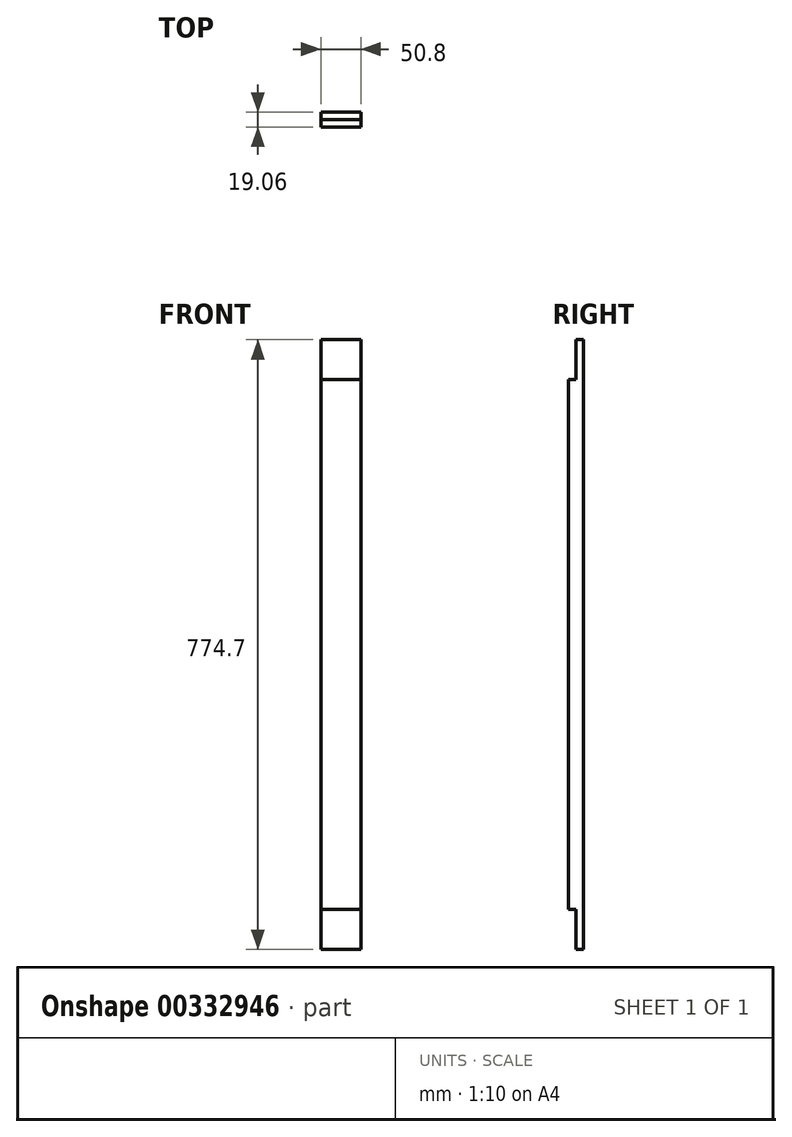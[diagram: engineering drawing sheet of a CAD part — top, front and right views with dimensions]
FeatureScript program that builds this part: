
annotation { "Feature Type Name" : "Feature", "Feature Type Description" : "" }
export const myFeature = defineFeature(function(context is Context, id is Id, definition is map)
    precondition{}
    {
        {
            var Q0;
            Q0=qCreatedBy(makeId("Top.planeOp"),FACE);
            var sketch = newSketch(context, id + "F0", { "sketchPlane" : qUnion([Q0])});
            skLineSegment(sketch, "E0.bottom", {"start": v(25.4, 9.53) * mm, "end": v(-25.4, 9.53) * mm});
            skLineSegment(sketch, "E0.top", {"start": v(25.4, -9.53) * mm, "end": v(-25.4, -9.53) * mm});
            skLineSegment(sketch, "E0.left", {"start": v(25.4, 9.53) * mm, "end": v(25.4, -9.52) * mm});
            skLineSegment(sketch, "E0.right", {"start": v(-25.4, 9.53) * mm, "end": v(-25.4, -9.53) * mm});
            skPoint(sketch, "E0.middle", {"position": v(0, 0) * mm});
            skSolve(sketch);
        }
        {
            var Q0;
            Q0=makeQuery(id+"F0.imprint","IMPRINT",FACE,{"disambiguationData":[TD([[makeQuery(id+"F0.imprint","IMPRINT",EDGE,{"derivedFrom":sQuery(id+"F0.wireOp",EDGE,"E0.bottom")}),1.0]])]});
            var Q1;
            Q1=qSketchRegion(id+"F2",true);
            extrude(context, id + "F1", {"entities" : qUnion([Q0, Q1]), "depth" : 774.7 * mm});
        }
        {
            var Q0;
            Q0=qCreatedBy(makeId("Front.planeOp"),FACE);
            var sketch = newSketch(context, id + "F2", { "sketchPlane" : qUnion([Q0])});
            skLineSegment(sketch, "E1.bottom", {"start": v(-38.77, 0) * mm, "end": v(83.66, 0) * mm});
            skLineSegment(sketch, "E1.top", {"start": v(-38.77, 50.8) * mm, "end": v(83.66, 50.8) * mm});
            skLineSegment(sketch, "E1.left", {"start": v(-38.77, 0) * mm, "end": v(-38.77, 50.8) * mm});
            skLineSegment(sketch, "E1.right", {"start": v(83.66, 0) * mm, "end": v(83.66, 50.8) * mm});
            skLineSegment(sketch, "E2.bottom", {"start": v(-210.36, 723.9) * mm, "end": v(132.8, 723.9) * mm});
            skLineSegment(sketch, "E2.top", {"start": v(-210.36, 774.7) * mm, "end": v(132.8, 774.7) * mm});
            skLineSegment(sketch, "E2.left", {"start": v(-210.36, 723.9) * mm, "end": v(-210.36, 774.7) * mm});
            skLineSegment(sketch, "E2.right", {"start": v(132.8, 723.9) * mm, "end": v(132.8, 774.7) * mm});
            skSolve(sketch);
        }
        {
            var Q0;
            Q0=qSketchRegion(id+"F2",true);
            extrude(context, id + "F3", {"entities" : qUnion([Q0]), "operationType" : NewBodyOperationType.REMOVE, "depth" : 25.4 * mm});
        }
    });
